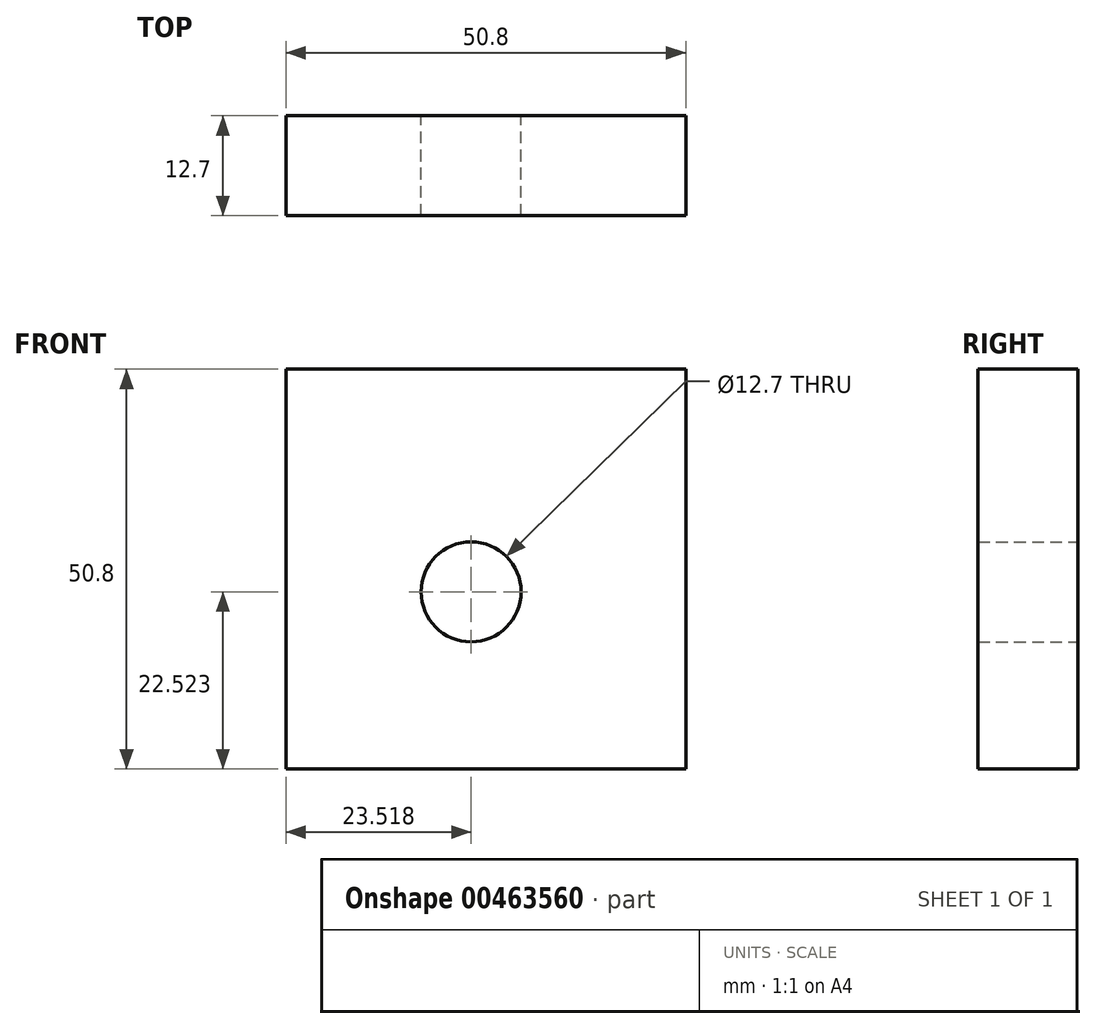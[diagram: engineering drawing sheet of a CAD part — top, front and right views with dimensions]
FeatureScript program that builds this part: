
annotation { "Feature Type Name" : "Feature", "Feature Type Description" : "" }
export const myFeature = defineFeature(function(context is Context, id is Id, definition is map)
    precondition{}
    {
        {
            var Q0;
            Q0=qCreatedBy(makeId("Front.planeOp"),FACE);
            var sketch = newSketch(context, id + "F0", { "sketchPlane" : qUnion([Q0])});
            skLineSegment(sketch, "E0.bottom", {"start": v(-17.33, 14.9) * mm, "end": v(33.47, 14.9) * mm});
            skLineSegment(sketch, "E0.top", {"start": v(-17.33, -35.9) * mm, "end": v(33.47, -35.9) * mm});
            skLineSegment(sketch, "E0.left", {"start": v(-17.33, 14.9) * mm, "end": v(-17.33, -35.9) * mm});
            skLineSegment(sketch, "E0.right", {"start": v(33.47, 14.9) * mm, "end": v(33.47, -35.9) * mm});
            skCircle(sketch, "E1", {"center": v(6.19, -13.39) * mm, "radius": 6.35 * mm});
            skSolve(sketch);
        }
        {
            var Q0;
            Q0 = qSketchRegion(id + "F0", true);
            extrude(context, id + "F1", {"entities" : qUnion([Q0]), "depth" : 12.7 * mm});
        }
    });
